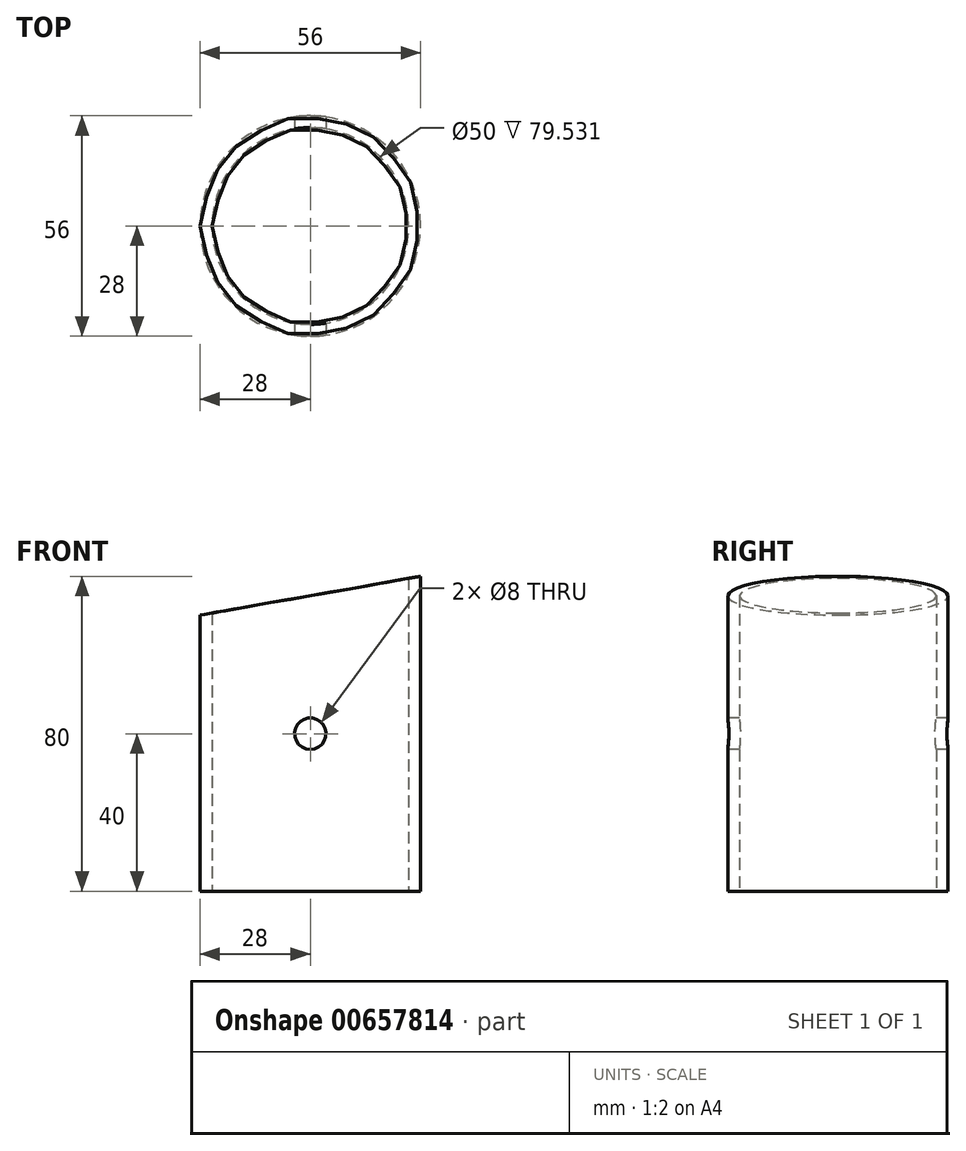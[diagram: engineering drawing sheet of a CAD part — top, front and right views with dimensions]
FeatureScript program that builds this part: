
annotation { "Feature Type Name" : "Feature", "Feature Type Description" : "" }
export const myFeature = defineFeature(function(context is Context, id is Id, definition is map)
    precondition{}
    {
        {
            var Q0;
            Q0=qCreatedBy(makeId("Top.planeOp"),FACE);
            var sketch = newSketch(context, id + "F0", { "sketchPlane" : qUnion([Q0])});
            skCircle(sketch, "E0", {"center": v(0, 0) * mm, "radius": 25 * mm});
            skCircle(sketch, "E1", {"center": v(0, 0) * mm, "radius": 28 * mm});
            skSolve(sketch);
        }
        {
            var Q0;
            Q0=makeQuery(id+"F0.imprint","IMPRINT",FACE,{"disambiguationData":[TD([[makeQuery(id+"F0.imprint","IMPRINT",EDGE,{"derivedFrom":sQuery(id+"F0.wireOp",EDGE,"E0")}),-1.0]])]});
            extrude(context, id + "F1", {"entities" : qUnion([Q0]), "depth" : 80 * mm, "offsetDistance" : 25 * mm});
        }
        {
            var Q0;
            Q0=qCreatedBy(makeId("Front.planeOp"),FACE);
            var sketch = newSketch(context, id + "F2", { "sketchPlane" : qUnion([Q0])});
            skLineSegment(sketch, "E2", {"start": v(-37, 68.54) * mm, "end": v(28, 80) * mm});
            skLineSegment(sketch, "E3", {"start": v(28, 80) * mm, "end": v(-37.07, 93.22) * mm});
            skLineSegment(sketch, "E4", {"start": v(-37.07, 93.22) * mm, "end": v(-37, 68.54) * mm});
            skPoint(sketch, "E5", {"position": v(28, 80) * mm});
            skSolve(sketch);
        }
        {
            var Q0;
            Q0=makeQuery(id+"F2.imprint","IMPRINT",FACE,{"disambiguationData":[TD([[makeQuery(id+"F2.imprint","IMPRINT",EDGE,{"derivedFrom":sQuery(id+"F2.wireOp",EDGE,"E2")}),1.0]])]});
            extrude(context, id + "F3", {"entities" : qUnion([Q0]), "operationType" : NewBodyOperationType.REMOVE, "oppositeDirection" : true, "depth" : 32.9 * mm, "offsetDistance" : 25 * mm, "hasSecondDirection" : true, "secondDirectionOppositeDirection" : false, "secondDirectionDepth" : 46.7 * mm});
        }
        {
            var Q0;
            Q0=qCreatedBy(makeId("Front.planeOp"),FACE);
            var sketch = newSketch(context, id + "F4", { "sketchPlane" : qUnion([Q0])});
            skCircle(sketch, "E6", {"center": v(0, 40) * mm, "radius": 4 * mm});
            skSolve(sketch);
        }
        {
            var Q0;
            Q0 = qSketchRegion(id + "F4", true);
            extrude(context, id + "F5", {"entities" : qUnion([Q0]), "operationType" : NewBodyOperationType.REMOVE, "oppositeDirection" : true, "depth" : 64.5 * mm, "offsetDistance" : 25 * mm, "hasSecondDirection" : true, "secondDirectionOppositeDirection" : false, "secondDirectionDepth" : 79.1 * mm});
        }
    });
